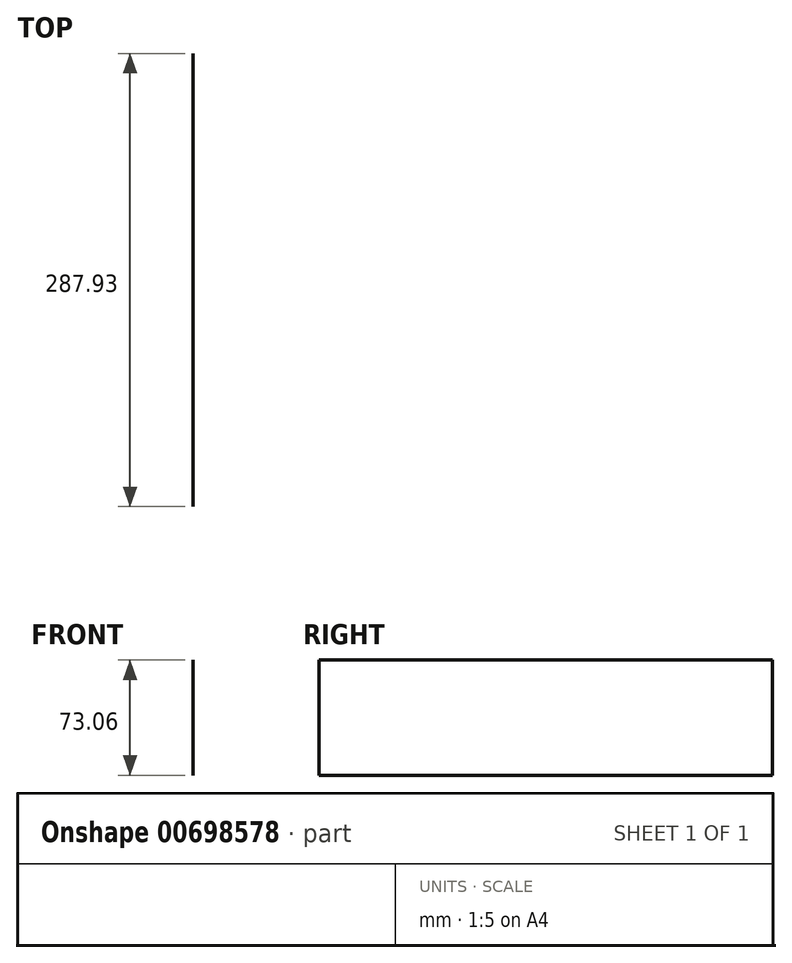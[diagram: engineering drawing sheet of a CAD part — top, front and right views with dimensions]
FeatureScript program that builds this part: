
annotation { "Feature Type Name" : "Feature", "Feature Type Description" : "" }
export const myFeature = defineFeature(function(context is Context, id is Id, definition is map)
    precondition{}
    {
        {
            var Q0;
            Q0=qCreatedBy(makeId("Front.planeOp"),FACE);
            var sketch = newSketch(context, id + "F0", { "sketchPlane" : qUnion([Q0])});
            skLineSegment(sketch, "E0.bottom", {"start": v(54.16, 48.96) * mm, "end": v(-51.18, 48.96) * mm});
            skLineSegment(sketch, "E0.top", {"start": v(54.16, -24.1) * mm, "end": v(-51.18, -24.1) * mm});
            skLineSegment(sketch, "E0.left", {"start": v(54.16, 48.96) * mm, "end": v(54.16, -24.1) * mm});
            skLineSegment(sketch, "E0.right", {"start": v(-51.18, 48.96) * mm, "end": v(-51.18, -24.1) * mm});
            skSolve(sketch);
        }
        {
            var Q0;
            Q0=makeQuery(id+"F0.imprint","IMPRINT",FACE,{"disambiguationData":[TD([[makeQuery(id+"F0.imprint","IMPRINT",EDGE,{"derivedFrom":sQuery(id+"F0.wireOp",EDGE,"E0.bottom")}),1.0]])]});
            var sketch = newSketch(context, id + "F1", { "sketchPlane" : qUnion([Q0])});
            skSolve(sketch);
        }
        {
            var Q0;
            Q0 = qSketchRegion(id + "F1", true);
            var Q1;
            Q1=sQuery(id+"F0.wireOp",EDGE,"E0.left");
            extrude(context, id + "F2", {"entities" : qUnion([Q0]), "bodyType" : ToolBodyType.SURFACE, "operationType" : NewBodyOperationType.ADD, "surfaceEntities" : qUnion([Q1]), "depth" : 287.93 * mm, "offsetDistance" : 25.4 * mm});
        }
    });
